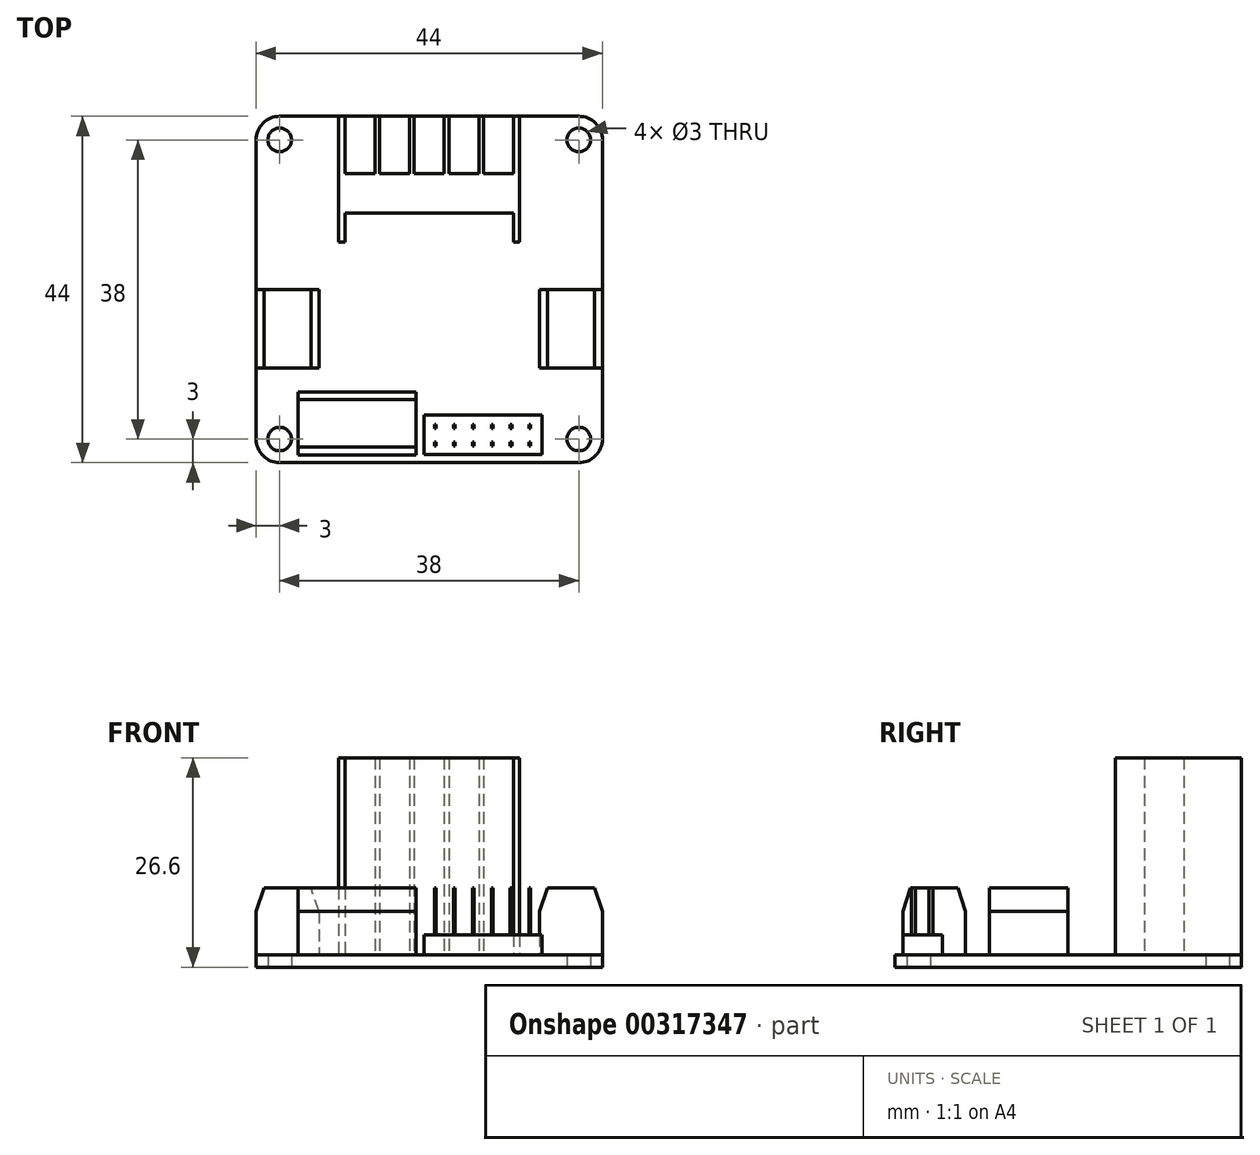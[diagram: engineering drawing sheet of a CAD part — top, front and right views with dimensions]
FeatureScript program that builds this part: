
annotation { "Feature Type Name" : "Feature", "Feature Type Description" : "" }
export const myFeature = defineFeature(function(context is Context, id is Id, definition is map)
    precondition{}
    {
        {
            var Q0;
            Q0=qCreatedBy(makeId("Top.planeOp"),FACE);
            var sketch = newSketch(context, id + "F0", { "sketchPlane" : qUnion([Q0])});
            skLineSegment(sketch, "E0.bottom", {"start": v(-19, 22) * mm, "end": v(19, 22) * mm});
            skLineSegment(sketch, "E0.top", {"start": v(-19, -22) * mm, "end": v(19, -22) * mm});
            skLineSegment(sketch, "E0.left", {"start": v(-22, 19) * mm, "end": v(-22, -19) * mm});
            skLineSegment(sketch, "E0.right", {"start": v(22, 19) * mm, "end": v(22, -19) * mm});
            skPoint(sketch, "E1.visualSharp", {"position": v(-22, 22) * mm});
            skArc(sketch, "E1.filletArc", {"start": v(-19, 22) * mm, "mid": v(-21.12, 21.12) * mm, "end": v(-22, 19) * mm});
            skPoint(sketch, "E2.visualSharp", {"position": v(22, 22) * mm});
            skArc(sketch, "E2.filletArc", {"start": v(22, 19) * mm, "mid": v(21.12, 21.12) * mm, "end": v(19, 22) * mm});
            skPoint(sketch, "E3.visualSharp", {"position": v(22, -22) * mm});
            skArc(sketch, "E3.filletArc", {"start": v(19, -22) * mm, "mid": v(21.12, -21.12) * mm, "end": v(22, -19) * mm});
            skPoint(sketch, "E4.visualSharp", {"position": v(-22, -22) * mm});
            skArc(sketch, "E4.filletArc", {"start": v(-22, -19) * mm, "mid": v(-21.12, -21.12) * mm, "end": v(-19, -22) * mm});
            skCircle(sketch, "E5", {"center": v(-19, 19) * mm, "radius": 1.5 * mm});
            skCircle(sketch, "E6.0.1.0", {"center": v(-19, -19) * mm, "radius": 1.5 * mm});
            skCircle(sketch, "E6.1.0.0", {"center": v(19, 19) * mm, "radius": 1.5 * mm});
            skCircle(sketch, "E6.1.1.0", {"center": v(19, -19) * mm, "radius": 1.5 * mm});
            skLineSegment(sketch, "E6.direction1", {"start": v(-19, 19) * mm, "end": v(19, 19) * mm, "construction": true});
            skLineSegment(sketch, "E6.direction2", {"start": v(-19, 19) * mm, "end": v(-19, -19) * mm, "construction": true});
            skSolve(sketch);
        }
        {
            var Q0;
            Q0=makeQuery(id+"F0.imprint","IMPRINT",FACE,{"disambiguationData":[TD([[makeQuery(id+"F0.imprint","IMPRINT",EDGE,{"derivedFrom":sQuery(id+"F0.wireOp",EDGE,"E0.bottom")}),-1.0]])]});
            extrude(context, id + "F1", {"entities" : qUnion([Q0]), "endBound" : BoundingType.SYMMETRIC, "depth" : 1.6 * mm});
        }
        {
            var Q0;
            Q0=makeQuery(id+"F1.opExtrude","CAP_FACE",FACE,{"disambiguationData":[OSD([sQuery(id+"F0.wireOp",EDGE,"E0.bottom"),sQuery(id+"F0.wireOp",EDGE,"E0.top"),sQuery(id+"F0.wireOp",EDGE,"E0.left"),sQuery(id+"F0.wireOp",EDGE,"E0.right"),sQuery(id+"F0.wireOp",EDGE,"E1.filletArc"),sQuery(id+"F0.wireOp",EDGE,"E2.filletArc"),sQuery(id+"F0.wireOp",EDGE,"E3.filletArc"),sQuery(id+"F0.wireOp",EDGE,"E4.filletArc"),sQuery(id+"F0.wireOp",EDGE,"E5"),sQuery(id+"F0.wireOp",EDGE,"E6.0.1.0"),sQuery(id+"F0.wireOp",EDGE,"E6.1.0.0"),sQuery(id+"F0.wireOp",EDGE,"E6.1.1.0")])],"isStart":false});
            var sketch = newSketch(context, id + "F2", { "sketchPlane" : qUnion([Q0])});
            skLineSegment(sketch, "E7.bottom", {"start": v(-11.5, 22) * mm, "end": v(11.5, 22) * mm});
            skLineSegment(sketch, "E7.left", {"start": v(-11.5, 22) * mm, "end": v(-11.5, 6) * mm});
            skLineSegment(sketch, "E7.right", {"start": v(11.5, 22) * mm, "end": v(11.5, 6) * mm});
            skLineSegment(sketch, "E8.bottom", {"start": v(-10.7, 22) * mm, "end": v(-6.9, 22) * mm});
            skLineSegment(sketch, "E8.top", {"start": v(-10.7, 14.7) * mm, "end": v(-6.9, 14.7) * mm});
            skLineSegment(sketch, "E8.left", {"start": v(-10.7, 22) * mm, "end": v(-10.7, 14.7) * mm});
            skLineSegment(sketch, "E8.right", {"start": v(-6.9, 22) * mm, "end": v(-6.9, 14.7) * mm});
            skLineSegment(sketch, "E9", {"start": v(-11.5, 14.7) * mm, "end": v(-10.7, 14.7) * mm, "construction": true});
            skLineSegment(sketch, "E10.1.0.0", {"start": v(-2.5, 22) * mm, "end": v(-2.5, 14.7) * mm});
            skLineSegment(sketch, "E10.1.0.1", {"start": v(-6.3, 14.7) * mm, "end": v(-2.5, 14.7) * mm});
            skLineSegment(sketch, "E10.1.0.2", {"start": v(-6.3, 22) * mm, "end": v(-6.3, 14.7) * mm});
            skLineSegment(sketch, "E10.1.0.3", {"start": v(-6.3, 22) * mm, "end": v(-2.5, 22) * mm});
            skLineSegment(sketch, "E10.2.0.0", {"start": v(1.9, 22) * mm, "end": v(1.9, 14.7) * mm});
            skLineSegment(sketch, "E10.2.0.1", {"start": v(-1.9, 14.7) * mm, "end": v(1.9, 14.7) * mm});
            skLineSegment(sketch, "E10.2.0.2", {"start": v(-1.9, 22) * mm, "end": v(-1.9, 14.7) * mm});
            skLineSegment(sketch, "E10.2.0.3", {"start": v(-1.9, 22) * mm, "end": v(1.9, 22) * mm});
            skLineSegment(sketch, "E10.3.0.0", {"start": v(6.3, 22) * mm, "end": v(6.3, 14.7) * mm});
            skLineSegment(sketch, "E10.3.0.1", {"start": v(2.5, 14.7) * mm, "end": v(6.3, 14.7) * mm});
            skLineSegment(sketch, "E10.3.0.2", {"start": v(2.5, 22) * mm, "end": v(2.5, 14.7) * mm});
            skLineSegment(sketch, "E10.3.0.3", {"start": v(2.5, 22) * mm, "end": v(6.3, 22) * mm});
            skLineSegment(sketch, "E10.4.0.0", {"start": v(10.7, 22) * mm, "end": v(10.7, 14.7) * mm});
            skLineSegment(sketch, "E10.4.0.1", {"start": v(6.9, 14.7) * mm, "end": v(10.7, 14.7) * mm});
            skLineSegment(sketch, "E10.4.0.2", {"start": v(6.9, 22) * mm, "end": v(6.9, 14.7) * mm});
            skLineSegment(sketch, "E10.4.0.3", {"start": v(6.9, 22) * mm, "end": v(10.7, 22) * mm});
            skLineSegment(sketch, "E10.direction1", {"start": v(-10.9, 14.7) * mm, "end": v(-6.5, 14.7) * mm, "construction": true});
            skLineSegment(sketch, "E11.top", {"start": v(-10.7, 9.71) * mm, "end": v(10.7, 9.71) * mm});
            skLineSegment(sketch, "E11.left", {"start": v(-10.7, 6) * mm, "end": v(-10.7, 9.71) * mm});
            skLineSegment(sketch, "E11.right", {"start": v(10.7, 6) * mm, "end": v(10.7, 9.71) * mm});
            skLineSegment(sketch, "E12", {"start": v(-11.5, 6) * mm, "end": v(-10.7, 6) * mm});
            skLineSegment(sketch, "E13", {"start": v(10.7, 6) * mm, "end": v(11.5, 6) * mm});
            skSolve(sketch);
        }
        {
            var Q0;
            {var subQ13=sQuery(id+"F2.wireOp",EDGE,"E7.left");Q0=makeQuery(id+"F2.imprint","IMPRINT",FACE,{"disambiguationData":[TD([[makeQuery(id+"F2.imprint","IMPRINT",EDGE,{"derivedFrom":subQ13}),1.0]])]});}
            extrude(context, id + "F3", {"entities" : qUnion([Q0]), "depth" : 25 * mm});
        }
        {
            var Q0;
            Q0=makeQuery(id+"F1.opExtrude","CAP_FACE",FACE,{"disambiguationData":[OSD([sQuery(id+"F0.wireOp",EDGE,"E0.bottom"),sQuery(id+"F0.wireOp",EDGE,"E0.top"),sQuery(id+"F0.wireOp",EDGE,"E0.left"),sQuery(id+"F0.wireOp",EDGE,"E0.right"),sQuery(id+"F0.wireOp",EDGE,"E1.filletArc"),sQuery(id+"F0.wireOp",EDGE,"E2.filletArc"),sQuery(id+"F0.wireOp",EDGE,"E3.filletArc"),sQuery(id+"F0.wireOp",EDGE,"E4.filletArc"),sQuery(id+"F0.wireOp",EDGE,"E5"),sQuery(id+"F0.wireOp",EDGE,"E6.0.1.0"),sQuery(id+"F0.wireOp",EDGE,"E6.1.0.0"),sQuery(id+"F0.wireOp",EDGE,"E6.1.1.0")])],"isStart":false});
            var sketch = newSketch(context, id + "F4", { "sketchPlane" : qUnion([Q0])});
            skLineSegment(sketch, "E14.bottom", {"start": v(-22, 0) * mm, "end": v(-14, 0) * mm});
            skLineSegment(sketch, "E14.top", {"start": v(-22, -10) * mm, "end": v(-14, -10) * mm});
            skLineSegment(sketch, "E14.left", {"start": v(-22, 0) * mm, "end": v(-22, -10) * mm});
            skLineSegment(sketch, "E14.right", {"start": v(-14, 0) * mm, "end": v(-14, -10) * mm});
            skLineSegment(sketch, "E15", {"start": v(-16.69, -22) * mm, "end": v(-16.69, -10) * mm, "construction": true});
            skLineSegment(sketch, "E16.MirrorCS", {"start": v(14, 0) * mm, "end": v(14, -10) * mm});
            skLineSegment(sketch, "E17.MirrorCS", {"start": v(22, 0) * mm, "end": v(14, 0) * mm});
            skLineSegment(sketch, "E18.MirrorCS", {"start": v(22, -10) * mm, "end": v(14, -10) * mm});
            skLineSegment(sketch, "E19.MirrorCS", {"start": v(22, 0) * mm, "end": v(22, -10) * mm});
            skLineSegment(sketch, "E20.bottom", {"start": v(-1.69, -13.01) * mm, "end": v(-16.69, -13.01) * mm});
            skLineSegment(sketch, "E20.top", {"start": v(-1.69, -21.01) * mm, "end": v(-16.69, -21.01) * mm});
            skLineSegment(sketch, "E20.left", {"start": v(-1.69, -13.01) * mm, "end": v(-1.69, -21.01) * mm});
            skLineSegment(sketch, "E20.right", {"start": v(-16.69, -13.01) * mm, "end": v(-16.69, -21.01) * mm});
            skSolve(sketch);
        }
        {
            var Q0;
            Q0=makeQuery(id+"F4.imprint","IMPRINT",FACE,{"disambiguationData":[TD([[makeQuery(id+"F4.imprint","IMPRINT",EDGE,{"derivedFrom":sQuery(id+"F4.wireOp",EDGE,"E20.bottom")}),1.0]])]});
            var Q1;
            Q1=makeQuery(id+"F4.imprint","IMPRINT",FACE,{"disambiguationData":[TD([[makeQuery(id+"F4.imprint","IMPRINT",EDGE,{"derivedFrom":sQuery(id+"F4.wireOp",EDGE,"E14.bottom")}),-1.0]])]});
            var Q2;
            Q2=makeQuery(id+"F4.imprint","IMPRINT",FACE,{"disambiguationData":[TD([[makeQuery(id+"F4.imprint","IMPRINT",EDGE,{"derivedFrom":sQuery(id+"F4.wireOp",EDGE,"E16.MirrorCS")}),1.0]])]});
            extrude(context, id + "F5", {"entities" : qUnion([Q0, Q1, Q2]), "depth" : 8.5 * mm});
        }
        {
            var Q0;
            Q0=makeQuery(id+"F5.opExtrude","CAP_EDGE",EDGE,{"disambiguationData":[OSD([sQuery(id+"F4.wireOp",EDGE,"E19.MirrorCS")])],"isStart":false});
            var Q1;
            Q1=makeQuery(id+"F5.opExtrude","CAP_EDGE",EDGE,{"disambiguationData":[OSD([sQuery(id+"F4.wireOp",EDGE,"E16.MirrorCS")])],"isStart":false});
            var Q2;
            Q2=makeQuery(id+"F5.opExtrude","CAP_EDGE",EDGE,{"disambiguationData":[OSD([sQuery(id+"F4.wireOp",EDGE,"E14.right")])],"isStart":false});
            var Q3;
            Q3=makeQuery(id+"F5.opExtrude","CAP_EDGE",EDGE,{"disambiguationData":[OSD([sQuery(id+"F4.wireOp",EDGE,"E20.top")])],"isStart":false});
            var Q4;
            Q4=makeQuery(id+"F5.opExtrude","CAP_EDGE",EDGE,{"disambiguationData":[OSD([sQuery(id+"F4.wireOp",EDGE,"E14.left")])],"isStart":false});
            var Q5;
            Q5=makeQuery(id+"F5.opExtrude","CAP_EDGE",EDGE,{"disambiguationData":[OSD([sQuery(id+"F4.wireOp",EDGE,"E20.bottom")])],"isStart":false});
            chamfer(context, id + "F6", {"entities" : qUnion([Q0, Q1, Q2, Q3, Q4, Q5]), "chamferType" : ChamferType.TWO_OFFSETS, "width1" : 3 * mm, "oppositeDirection" : false, "width2" : 1 * mm, "tangentPropagation" : true});
        }
        {
            var Q0;
            Q0=makeQuery(id+"F1.opExtrude","CAP_FACE",FACE,{"disambiguationData":[OSD([sQuery(id+"F0.wireOp",EDGE,"E0.bottom"),sQuery(id+"F0.wireOp",EDGE,"E0.top"),sQuery(id+"F0.wireOp",EDGE,"E0.left"),sQuery(id+"F0.wireOp",EDGE,"E0.right"),sQuery(id+"F0.wireOp",EDGE,"E1.filletArc"),sQuery(id+"F0.wireOp",EDGE,"E2.filletArc"),sQuery(id+"F0.wireOp",EDGE,"E3.filletArc"),sQuery(id+"F0.wireOp",EDGE,"E4.filletArc"),sQuery(id+"F0.wireOp",EDGE,"E5"),sQuery(id+"F0.wireOp",EDGE,"E6.0.1.0"),sQuery(id+"F0.wireOp",EDGE,"E6.1.0.0"),sQuery(id+"F0.wireOp",EDGE,"E6.1.1.0")])],"isStart":false});
            var sketch = newSketch(context, id + "F7", { "sketchPlane" : qUnion([Q0])});
            skLineSegment(sketch, "E21.bottom", {"start": v(-0.66, -15.97) * mm, "end": v(14.34, -15.97) * mm});
            skLineSegment(sketch, "E21.top", {"start": v(-0.66, -20.97) * mm, "end": v(14.34, -20.97) * mm});
            skLineSegment(sketch, "E21.left", {"start": v(-0.66, -15.97) * mm, "end": v(-0.66, -20.97) * mm});
            skLineSegment(sketch, "E21.right", {"start": v(14.34, -15.97) * mm, "end": v(14.34, -20.97) * mm});
            skSolve(sketch);
        }
        {
            var Q0;
            Q0=makeQuery(id+"F7.imprint","IMPRINT",FACE,{"disambiguationData":[TD([[makeQuery(id+"F7.imprint","IMPRINT",EDGE,{"derivedFrom":sQuery(id+"F7.wireOp",EDGE,"E21.bottom")}),-1.0]])]});
            extrude(context, id + "F8", {"entities" : qUnion([Q0]), "depth" : 2.5 * mm});
        }
        {
            var Q0;
            Q0=makeQuery(id+"F8.opExtrude","CAP_FACE",FACE,{"disambiguationData":[OSD([sQuery(id+"F7.wireOp",EDGE,"E21.bottom"),sQuery(id+"F7.wireOp",EDGE,"E21.top"),sQuery(id+"F7.wireOp",EDGE,"E21.left"),sQuery(id+"F7.wireOp",EDGE,"E21.right")])],"isStart":false});
            var sketch = newSketch(context, id + "F9", { "sketchPlane" : qUnion([Q0])});
            skLineSegment(sketch, "E22.bottom", {"start": v(0.7, -19.39) * mm, "end": v(0.9, -19.39) * mm});
            skLineSegment(sketch, "E22.top", {"start": v(0.7, -19.89) * mm, "end": v(0.9, -19.89) * mm});
            skLineSegment(sketch, "E22.left", {"start": v(0.7, -19.39) * mm, "end": v(0.7, -19.89) * mm});
            skLineSegment(sketch, "E22.right", {"start": v(0.9, -19.39) * mm, "end": v(0.9, -19.89) * mm});
            skLineSegment(sketch, "E23.0.1.0", {"start": v(0.9, -17.19) * mm, "end": v(0.9, -17.69) * mm});
            skLineSegment(sketch, "E23.0.1.1", {"start": v(0.7, -17.69) * mm, "end": v(0.9, -17.69) * mm});
            skLineSegment(sketch, "E23.0.1.2", {"start": v(0.7, -17.19) * mm, "end": v(0.7, -17.69) * mm});
            skLineSegment(sketch, "E23.0.1.3", {"start": v(0.7, -17.19) * mm, "end": v(0.9, -17.19) * mm});
            skLineSegment(sketch, "E23.1.0.0", {"start": v(3.3, -19.39) * mm, "end": v(3.3, -19.89) * mm});
            skLineSegment(sketch, "E23.1.0.1", {"start": v(3.1, -19.89) * mm, "end": v(3.3, -19.89) * mm});
            skLineSegment(sketch, "E23.1.0.2", {"start": v(3.1, -19.39) * mm, "end": v(3.1, -19.89) * mm});
            skLineSegment(sketch, "E23.1.0.3", {"start": v(3.1, -19.39) * mm, "end": v(3.3, -19.39) * mm});
            skLineSegment(sketch, "E23.1.1.0", {"start": v(3.3, -17.19) * mm, "end": v(3.3, -17.69) * mm});
            skLineSegment(sketch, "E23.1.1.1", {"start": v(3.1, -17.69) * mm, "end": v(3.3, -17.69) * mm});
            skLineSegment(sketch, "E23.1.1.2", {"start": v(3.1, -17.19) * mm, "end": v(3.1, -17.69) * mm});
            skLineSegment(sketch, "E23.1.1.3", {"start": v(3.1, -17.19) * mm, "end": v(3.3, -17.19) * mm});
            skLineSegment(sketch, "E23.2.0.0", {"start": v(5.7, -19.39) * mm, "end": v(5.7, -19.89) * mm});
            skLineSegment(sketch, "E23.2.0.1", {"start": v(5.5, -19.89) * mm, "end": v(5.7, -19.89) * mm});
            skLineSegment(sketch, "E23.2.0.2", {"start": v(5.5, -19.39) * mm, "end": v(5.5, -19.89) * mm});
            skLineSegment(sketch, "E23.2.0.3", {"start": v(5.5, -19.39) * mm, "end": v(5.7, -19.39) * mm});
            skLineSegment(sketch, "E23.2.1.0", {"start": v(5.7, -17.19) * mm, "end": v(5.7, -17.69) * mm});
            skLineSegment(sketch, "E23.2.1.1", {"start": v(5.5, -17.69) * mm, "end": v(5.7, -17.69) * mm});
            skLineSegment(sketch, "E23.2.1.2", {"start": v(5.5, -17.19) * mm, "end": v(5.5, -17.69) * mm});
            skLineSegment(sketch, "E23.2.1.3", {"start": v(5.5, -17.19) * mm, "end": v(5.7, -17.19) * mm});
            skLineSegment(sketch, "E23.3.0.0", {"start": v(8.1, -19.39) * mm, "end": v(8.1, -19.89) * mm});
            skLineSegment(sketch, "E23.3.0.1", {"start": v(7.9, -19.89) * mm, "end": v(8.1, -19.89) * mm});
            skLineSegment(sketch, "E23.3.0.2", {"start": v(7.9, -19.39) * mm, "end": v(7.9, -19.89) * mm});
            skLineSegment(sketch, "E23.3.0.3", {"start": v(7.9, -19.39) * mm, "end": v(8.1, -19.39) * mm});
            skLineSegment(sketch, "E23.3.1.0", {"start": v(8.1, -17.19) * mm, "end": v(8.1, -17.69) * mm});
            skLineSegment(sketch, "E23.3.1.1", {"start": v(7.9, -17.69) * mm, "end": v(8.1, -17.69) * mm});
            skLineSegment(sketch, "E23.3.1.2", {"start": v(7.9, -17.19) * mm, "end": v(7.9, -17.69) * mm});
            skLineSegment(sketch, "E23.3.1.3", {"start": v(7.9, -17.19) * mm, "end": v(8.1, -17.19) * mm});
            skLineSegment(sketch, "E23.4.0.0", {"start": v(10.5, -19.39) * mm, "end": v(10.5, -19.89) * mm});
            skLineSegment(sketch, "E23.4.0.1", {"start": v(10.3, -19.89) * mm, "end": v(10.5, -19.89) * mm});
            skLineSegment(sketch, "E23.4.0.2", {"start": v(10.3, -19.39) * mm, "end": v(10.3, -19.89) * mm});
            skLineSegment(sketch, "E23.4.0.3", {"start": v(10.3, -19.39) * mm, "end": v(10.5, -19.39) * mm});
            skLineSegment(sketch, "E23.4.1.0", {"start": v(10.5, -17.19) * mm, "end": v(10.5, -17.69) * mm});
            skLineSegment(sketch, "E23.4.1.1", {"start": v(10.3, -17.69) * mm, "end": v(10.5, -17.69) * mm});
            skLineSegment(sketch, "E23.4.1.2", {"start": v(10.3, -17.19) * mm, "end": v(10.3, -17.69) * mm});
            skLineSegment(sketch, "E23.4.1.3", {"start": v(10.3, -17.19) * mm, "end": v(10.5, -17.19) * mm});
            skLineSegment(sketch, "E23.5.0.0", {"start": v(12.9, -19.39) * mm, "end": v(12.9, -19.89) * mm});
            skLineSegment(sketch, "E23.5.0.1", {"start": v(12.7, -19.89) * mm, "end": v(12.9, -19.89) * mm});
            skLineSegment(sketch, "E23.5.0.2", {"start": v(12.7, -19.39) * mm, "end": v(12.7, -19.89) * mm});
            skLineSegment(sketch, "E23.5.0.3", {"start": v(12.7, -19.39) * mm, "end": v(12.9, -19.39) * mm});
            skLineSegment(sketch, "E23.5.1.0", {"start": v(12.9, -17.19) * mm, "end": v(12.9, -17.69) * mm});
            skLineSegment(sketch, "E23.5.1.1", {"start": v(12.7, -17.69) * mm, "end": v(12.9, -17.69) * mm});
            skLineSegment(sketch, "E23.5.1.2", {"start": v(12.7, -17.19) * mm, "end": v(12.7, -17.69) * mm});
            skLineSegment(sketch, "E23.5.1.3", {"start": v(12.7, -17.19) * mm, "end": v(12.9, -17.19) * mm});
            skLineSegment(sketch, "E23.direction1", {"start": v(0.7, -19.89) * mm, "end": v(3.1, -19.89) * mm, "construction": true});
            skLineSegment(sketch, "E23.direction2", {"start": v(0.7, -19.89) * mm, "end": v(0.7, -17.69) * mm, "construction": true});
            skSolve(sketch);
        }
        {
            var Q0;
            Q0=makeQuery(id+"F9.imprint","IMPRINT",FACE,{"disambiguationData":[TD([[makeQuery(id+"F9.imprint","IMPRINT",EDGE,{"derivedFrom":sQuery(id+"F9.wireOp",EDGE,"E22.bottom")}),-1.0]])]});
            var Q1;
            Q1=makeQuery(id+"F9.imprint","IMPRINT",FACE,{"disambiguationData":[TD([[makeQuery(id+"F9.imprint","IMPRINT",EDGE,{"derivedFrom":sQuery(id+"F9.wireOp",EDGE,"E23.0.1.0")}),-1.0]])]});
            var Q2;
            Q2=makeQuery(id+"F9.imprint","IMPRINT",FACE,{"disambiguationData":[TD([[makeQuery(id+"F9.imprint","IMPRINT",EDGE,{"derivedFrom":sQuery(id+"F9.wireOp",EDGE,"E23.1.1.0")}),-1.0]])]});
            var Q3;
            Q3=makeQuery(id+"F9.imprint","IMPRINT",FACE,{"disambiguationData":[TD([[makeQuery(id+"F9.imprint","IMPRINT",EDGE,{"derivedFrom":sQuery(id+"F9.wireOp",EDGE,"E23.1.0.0")}),-1.0]])]});
            var Q4;
            Q4=makeQuery(id+"F9.imprint","IMPRINT",FACE,{"disambiguationData":[TD([[makeQuery(id+"F9.imprint","IMPRINT",EDGE,{"derivedFrom":sQuery(id+"F9.wireOp",EDGE,"E23.2.0.0")}),-1.0]])]});
            var Q5;
            Q5=makeQuery(id+"F9.imprint","IMPRINT",FACE,{"disambiguationData":[TD([[makeQuery(id+"F9.imprint","IMPRINT",EDGE,{"derivedFrom":sQuery(id+"F9.wireOp",EDGE,"E23.2.1.0")}),-1.0]])]});
            var Q6;
            Q6=makeQuery(id+"F9.imprint","IMPRINT",FACE,{"disambiguationData":[TD([[makeQuery(id+"F9.imprint","IMPRINT",EDGE,{"derivedFrom":sQuery(id+"F9.wireOp",EDGE,"E23.3.1.0")}),-1.0]])]});
            var Q7;
            Q7=makeQuery(id+"F9.imprint","IMPRINT",FACE,{"disambiguationData":[TD([[makeQuery(id+"F9.imprint","IMPRINT",EDGE,{"derivedFrom":sQuery(id+"F9.wireOp",EDGE,"E23.3.0.0")}),-1.0]])]});
            var Q8;
            Q8=makeQuery(id+"F9.imprint","IMPRINT",FACE,{"disambiguationData":[TD([[makeQuery(id+"F9.imprint","IMPRINT",EDGE,{"derivedFrom":sQuery(id+"F9.wireOp",EDGE,"E23.4.0.0")}),-1.0]])]});
            var Q9;
            Q9=makeQuery(id+"F9.imprint","IMPRINT",FACE,{"disambiguationData":[TD([[makeQuery(id+"F9.imprint","IMPRINT",EDGE,{"derivedFrom":sQuery(id+"F9.wireOp",EDGE,"E23.4.1.0")}),-1.0]])]});
            var Q10;
            Q10=makeQuery(id+"F9.imprint","IMPRINT",FACE,{"disambiguationData":[TD([[makeQuery(id+"F9.imprint","IMPRINT",EDGE,{"derivedFrom":sQuery(id+"F9.wireOp",EDGE,"E23.5.1.0")}),-1.0]])]});
            var Q11;
            Q11=makeQuery(id+"F9.imprint","IMPRINT",FACE,{"disambiguationData":[TD([[makeQuery(id+"F9.imprint","IMPRINT",EDGE,{"derivedFrom":sQuery(id+"F9.wireOp",EDGE,"E23.5.0.0")}),-1.0]])]});
            extrude(context, id + "F10", {"entities" : qUnion([Q0, Q1, Q2, Q3, Q4, Q5, Q6, Q7, Q8, Q9, Q10, Q11]), "operationType" : NewBodyOperationType.ADD, "depth" : 6 * mm});
        }
    });
